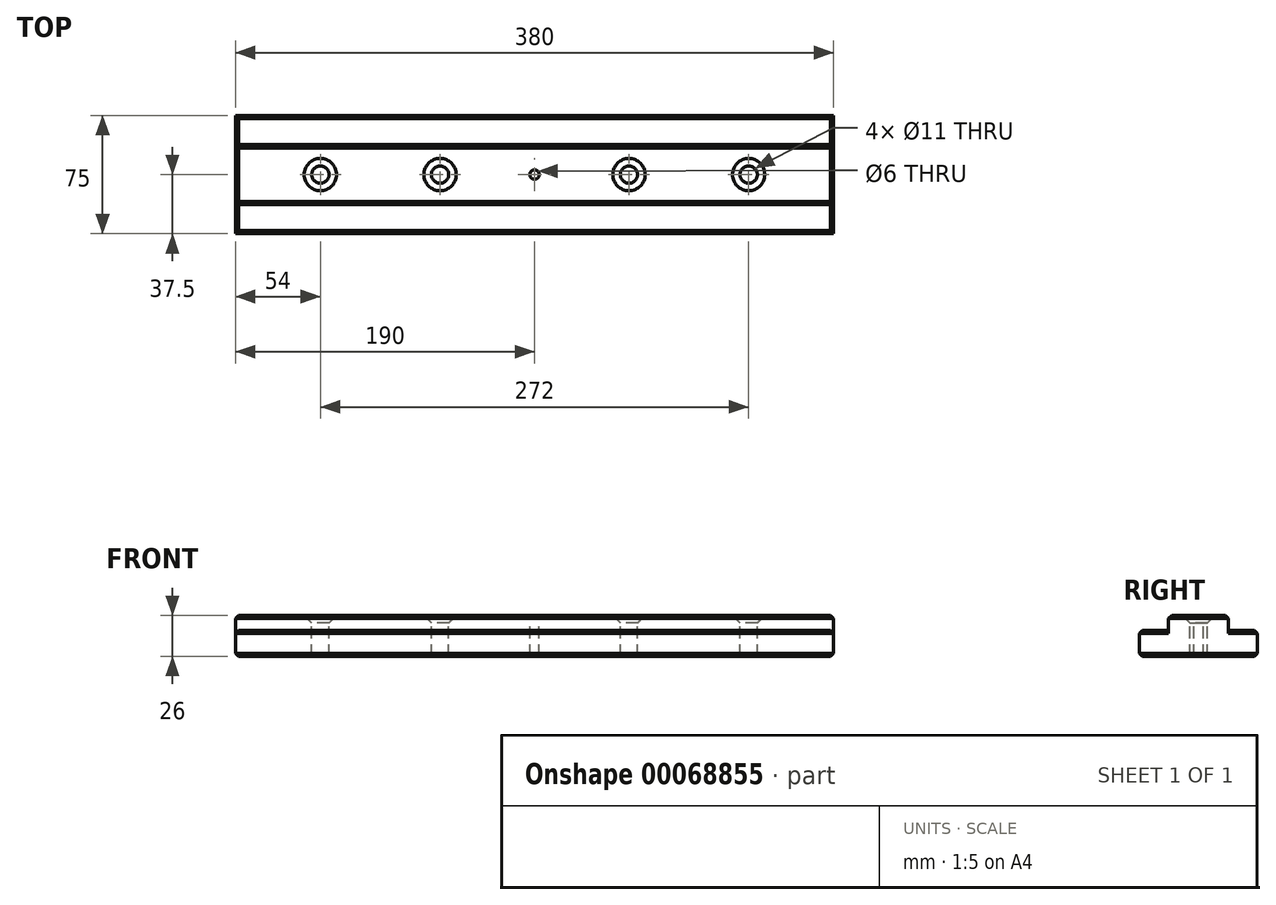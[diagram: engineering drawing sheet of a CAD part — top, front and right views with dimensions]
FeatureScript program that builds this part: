
annotation { "Feature Type Name" : "Feature", "Feature Type Description" : "" }
export const myFeature = defineFeature(function(context is Context, id is Id, definition is map)
    precondition{}
    {
        {
            var Q0;
            Q0=qCreatedBy(makeId("Right.planeOp"),FACE);
            var sketch = newSketch(context, id + "F0", { "sketchPlane" : qUnion([Q0])});
            skLineSegment(sketch, "E0.rect.bottom", {"start": v(-19, 13) * mm, "end": v(19, 13) * mm});
            skLineSegment(sketch, "E0.rect.top", {"start": v(-37.5, -13) * mm, "end": v(37.5, -13) * mm});
            skLineSegment(sketch, "E0.rect.left", {"start": v(-37.5, 3.5) * mm, "end": v(-37.5, -13) * mm});
            skLineSegment(sketch, "E0.rect.right", {"start": v(37.5, 3.5) * mm, "end": v(37.5, -13) * mm});
            skPoint(sketch, "E0.rect.middle", {"position": v(0, 0) * mm});
            skLineSegment(sketch, "E1.top", {"start": v(-37.5, 3.5) * mm, "end": v(-19, 3.5) * mm});
            skLineSegment(sketch, "E1.right", {"start": v(-19, 13) * mm, "end": v(-19, 3.5) * mm});
            skLineSegment(sketch, "E2.top", {"start": v(37.5, 3.5) * mm, "end": v(19, 3.5) * mm});
            skLineSegment(sketch, "E2.right", {"start": v(19, 13) * mm, "end": v(19, 3.5) * mm});
            skPoint(sketch, "E3.orphan", {"position": v(-37.5, 13) * mm});
            skPoint(sketch, "E4.orphan", {"position": v(37.5, 13) * mm});
            skSolve(sketch);
        }
        {
            var Q0;
            Q0 = qSketchRegion(id + "F0", true);
            extrude(context, id + "F1", {"entities" : qUnion([Q0]), "endBound" : BoundingType.SYMMETRIC, "depth" : 380 * mm});
        }
        {
            var Q0;
            Q0=makeQuery(id+"F1.opExtrude","SWEPT_FACE",FACE,{"disambiguationData":[OSD([sQuery(id+"F0.wireOp",EDGE,"E0.rect.top")])]});
            var Q1;
            Q1=makeQuery(id+"F1.opExtrude","SWEPT_FACE",FACE,{"disambiguationData":[OSD([sQuery(id+"F0.wireOp",EDGE,"E0.rect.bottom")])]});
            var Q2;
            Q2=makeQuery(id+"F1.opExtrude","SWEPT_EDGE",EDGE,{"disambiguationData":[OSD([sQuery(id+"F0.wireOp",EDGE,"E0.rect.left"),sQuery(id+"F0.wireOp",EDGE,"E1.top")])]});
            var Q3;
            Q3=makeQuery(id+"F1.opExtrude","SWEPT_EDGE",EDGE,{"disambiguationData":[OSD([sQuery(id+"F0.wireOp",EDGE,"E0.rect.right"),sQuery(id+"F0.wireOp",EDGE,"E2.top")])]});
            var Q4;
            Q4=makeQuery(id+"F1.opExtrude","CAP_EDGE",EDGE,{"disambiguationData":[OSD([sQuery(id+"F0.wireOp",EDGE,"E2.top")])],"isStart":false});
            var Q5;
            Q5=makeQuery(id+"F1.opExtrude","CAP_EDGE",EDGE,{"disambiguationData":[OSD([sQuery(id+"F0.wireOp",EDGE,"E1.top")])],"isStart":false});
            var Q6;
            Q6=makeQuery(id+"F1.opExtrude","CAP_EDGE",EDGE,{"disambiguationData":[OSD([sQuery(id+"F0.wireOp",EDGE,"E1.top")])],"isStart":true});
            var Q7;
            Q7=makeQuery(id+"F1.opExtrude","CAP_EDGE",EDGE,{"disambiguationData":[OSD([sQuery(id+"F0.wireOp",EDGE,"E2.top")])],"isStart":true});
            chamfer(context, id + "F2", {"entities" : qUnion([Q0, Q1, Q2, Q3, Q4, Q5, Q6, Q7]), "width" : 2 * mm, "tangentPropagation" : true});
        }
        {
            var Q0;
            Q0=makeQuery(id+"F1.opExtrude","SWEPT_FACE",FACE,{"disambiguationData":[OSD([sQuery(id+"F0.wireOp",EDGE,"E0.rect.bottom")])]});
            var sketch = newSketch(context, id + "F3", { "sketchPlane" : qUnion([Q0])});
            skLineSegment(sketch, "E5", {"start": v(-223.42, 0) * mm, "end": v(215.21, 0) * mm, "construction": true});
            skLineSegment(sketch, "E6", {"start": v(0, 111.52) * mm, "end": v(0, -105.56) * mm, "construction": true});
            skLineSegment(sketch, "E7.0", {"start": v(-60, 111.52) * mm, "end": v(-60, -105.56) * mm, "construction": true});
            skLineSegment(sketch, "E8.0", {"start": v(-136, 111.52) * mm, "end": v(-136, -105.56) * mm, "construction": true});
            skPoint(sketch, "E9", {"position": v(-136, 0) * mm});
            skPoint(sketch, "E10", {"position": v(-60, 0) * mm});
            skPoint(sketch, "E11", {"position": v(0, 0) * mm});
            skPoint(sketch, "E12.MirrorP", {"position": v(60, 0) * mm});
            skPoint(sketch, "E13.MirrorP", {"position": v(136, 0) * mm});
            skSolve(sketch);
        }
        {
            var Q0;
            Q0=sQuery(id+"F3.wireOp",VERTEX,"E11");
            var Q1;
            Q1=makeQuery(id+"F1.opExtrude","SWEPT_BODY",BODY,{"disambiguationData":[OSD([sQuery(id+"F0.wireOp",EDGE,"E0.rect.bottom"),sQuery(id+"F0.wireOp",EDGE,"E0.rect.top"),sQuery(id+"F0.wireOp",EDGE,"E0.rect.left"),sQuery(id+"F0.wireOp",EDGE,"E0.rect.right"),sQuery(id+"F0.wireOp",EDGE,"E1.top"),sQuery(id+"F0.wireOp",EDGE,"E1.right"),sQuery(id+"F0.wireOp",EDGE,"E2.top"),sQuery(id+"F0.wireOp",EDGE,"E2.right")])]});
            hole(context, id + "F4", {"style" : HoleStyle.SIMPLE, "holeDiameter" : 6 * mm, "endStyle" : HoleEndStyle.THROUGH, "locations" : qUnion([Q0]), "scope" : qUnion([Q1])});
        }
        {
            var Q0;
            Q0=sQuery(id+"F3.wireOp",VERTEX,"E9");
            var Q1;
            Q1=sQuery(id+"F3.wireOp",VERTEX,"E10");
            var Q2;
            Q2=sQuery(id+"F3.wireOp",VERTEX,"E12.MirrorP");
            var Q3;
            Q3=sQuery(id+"F3.wireOp",VERTEX,"E13.MirrorP");
            var Q4;
            Q4=makeQuery(id+"F1.opExtrude","SWEPT_BODY",BODY,{"disambiguationData":[OSD([sQuery(id+"F0.wireOp",EDGE,"E0.rect.bottom"),sQuery(id+"F0.wireOp",EDGE,"E0.rect.top"),sQuery(id+"F0.wireOp",EDGE,"E0.rect.left"),sQuery(id+"F0.wireOp",EDGE,"E0.rect.right"),sQuery(id+"F0.wireOp",EDGE,"E1.top"),sQuery(id+"F0.wireOp",EDGE,"E1.right"),sQuery(id+"F0.wireOp",EDGE,"E2.top"),sQuery(id+"F0.wireOp",EDGE,"E2.right")])]});
            hole(context, id + "F5", {"style" : HoleStyle.C_SINK, "holeDiameter" : 11 * mm, "cSinkDiameter" : 20.5 * mm, "endStyle" : HoleEndStyle.THROUGH, "locations" : qUnion([Q0, Q1, Q2, Q3]), "scope" : qUnion([Q4]), "cSinkAngle" : 90 * degree});
        }
    });
